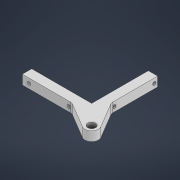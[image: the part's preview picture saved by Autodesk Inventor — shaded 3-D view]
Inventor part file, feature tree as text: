
AUTODESK INVENTOR PART (.ipt)
format: ipt  version: 2022 (Build 260153000, 153)  size: 137,728 bytes
history: native  units: mm
features: extrude x3, sketch x3
ambient origin geometry x8: Origin, YZ Plane, XZ Plane, XY Plane, X Axis, Y Axis, Z Axis, Center Point
bodies: Solid1 (feature_tree)
feature tree (6):
  extrude  "Extrusion1"  Depth=25.0mm
  extrude  "Extrusion2"  Depth=7.0mm
  extrude  "Extrusion3"  TaperAngle=135.0deg  [1 undecoded]
  sketch  "Sketch1"  dims[d0=35.0mm d2=25.0mm]
  sketch  "Sketch2"  dims[d3=45.0mm d4=7.0mm]
  sketch  "Sketch3"  dims[d5=7.0mm d6=135.0deg d7=6.0mm d8=10.0mm d9=4.0mm d10=7.0mm d11=0.0mm d12=10.0mm d13=30.0mm d14=2.5mm d15=2.5mm d16=7.0mm d17=0.0mm d18=10.0mm d19=30.0mm d20=2.5mm d21=2.5mm d22=10.0mm d23=0.0mm]
note: 1 required parameter value undecoded (feature->parameter linkage not recoverable at this tier; creation-order binding heuristic only, values carry confidence <= 0.55)
